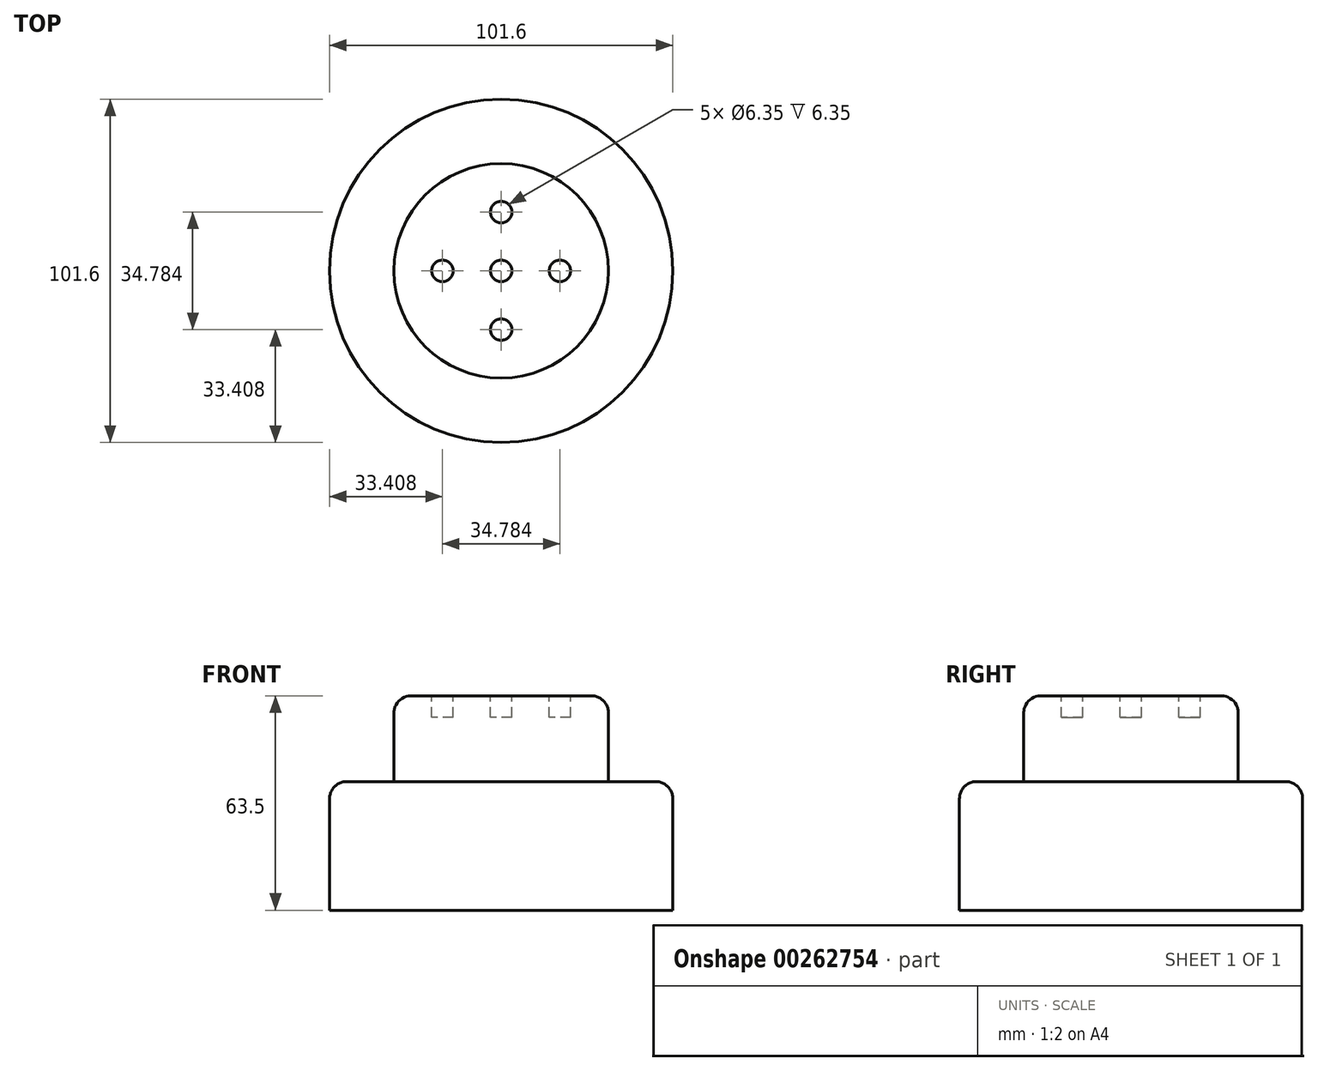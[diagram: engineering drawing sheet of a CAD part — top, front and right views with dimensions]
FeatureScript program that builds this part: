
annotation { "Feature Type Name" : "Feature", "Feature Type Description" : "" }
export const myFeature = defineFeature(function(context is Context, id is Id, definition is map)
    precondition{}
    {
        {
            var Q0;
            Q0=qCreatedBy(makeId("Top.planeOp"),FACE);
            var sketch = newSketch(context, id + "F0", { "sketchPlane" : qUnion([Q0])});
            skCircle(sketch, "E0", {"center": v(0, 0) * mm, "radius": 50.8 * mm});
            skSolve(sketch);
        }
        {
            var Q0;
            Q0=makeQuery(id+"F0.imprint","IMPRINT",FACE,{"disambiguationData":[TD([[makeQuery(id+"F0.imprint","IMPRINT",EDGE,{"derivedFrom":sQuery(id+"F0.wireOp",EDGE,"E0")}),1.0]])]});
            extrude(context, id + "F1", {"entities" : qUnion([Q0]), "depth" : 38.1 * mm});
        }
        {
            var Q0;
            Q0=makeQuery(id+"F1.opExtrude","CAP_FACE",FACE,{"disambiguationData":[OSD([sQuery(id+"F0.wireOp",EDGE,"E0")])],"isStart":false});
            var sketch = newSketch(context, id + "F2", { "sketchPlane" : qUnion([Q0])});
            skCircle(sketch, "E1", {"center": v(0, 0) * mm, "radius": 31.75 * mm});
            skSolve(sketch);
        }
        {
            var Q0;
            Q0 = qSketchRegion(id + "F2", true);
            extrude(context, id + "F3", {"entities" : qUnion([Q0]), "operationType" : NewBodyOperationType.ADD, "depth" : 25.4 * mm});
        }
        {
            var Q0;
            Q0=makeQuery(id+"F3.opExtrude","CAP_FACE",FACE,{"disambiguationData":[OSD([sQuery(id+"F2.wireOp",EDGE,"E1")])],"isStart":false});
            var sketch = newSketch(context, id + "F4", { "sketchPlane" : qUnion([Q0])});
            skLineSegment(sketch, "E2", {"start": v(0, 0) * mm, "end": v(0, 31.75) * mm, "construction": true});
            skLineSegment(sketch, "E3", {"start": v(0, 0) * mm, "end": v(31.75, 0) * mm, "construction": true});
            skLineSegment(sketch, "E4", {"start": v(0, 0) * mm, "end": v(0, -31.75) * mm, "construction": true});
            skLineSegment(sketch, "E5", {"start": v(0, 0) * mm, "end": v(-31.75, 0) * mm, "construction": true});
            skCircle(sketch, "E6", {"center": v(0, 0) * mm, "radius": 17.4 * mm, "construction": true});
            skPoint(sketch, "E7", {"position": v(-17.4, 0) * mm});
            skPoint(sketch, "E8", {"position": v(0, -17.4) * mm});
            skPoint(sketch, "E9", {"position": v(17.4, 0) * mm});
            skPoint(sketch, "E10", {"position": v(0, 17.4) * mm});
            skCircle(sketch, "E11", {"center": v(-17.4, 0) * mm, "radius": 3.18 * mm});
            skCircle(sketch, "E12", {"center": v(0, -17.4) * mm, "radius": 3.18 * mm});
            skCircle(sketch, "E13", {"center": v(17.4, 0) * mm, "radius": 3.18 * mm});
            skCircle(sketch, "E14", {"center": v(0, 17.4) * mm, "radius": 3.18 * mm});
            skCircle(sketch, "E15", {"center": v(0, 0) * mm, "radius": 3.18 * mm});
            skSolve(sketch);
        }
        {
            var Q0;
            Q0 = qSketchRegion(id + "F4", true);
            extrude(context, id + "F5", {"entities" : qUnion([Q0]), "operationType" : NewBodyOperationType.REMOVE, "oppositeDirection" : true, "depth" : 6.35 * mm});
        }
        {
            var Q0;
            Q0=makeQuery(id+"F3.opExtrude","CAP_EDGE",EDGE,{"disambiguationData":[OSD([sQuery(id+"F2.wireOp",EDGE,"E1")])],"isStart":false});
            var Q1;
            Q1=makeQuery(id+"F1.opExtrude","CAP_EDGE",EDGE,{"disambiguationData":[OSD([sQuery(id+"F0.wireOp",EDGE,"E0")])],"isStart":false});
            fillet(context, id + "F6", {"entities" : qUnion([Q0, Q1]), "radius" : 5.08 * mm, "tangentPropagation" : true, "allowEdgeOverflow" : false});
        }
    });
